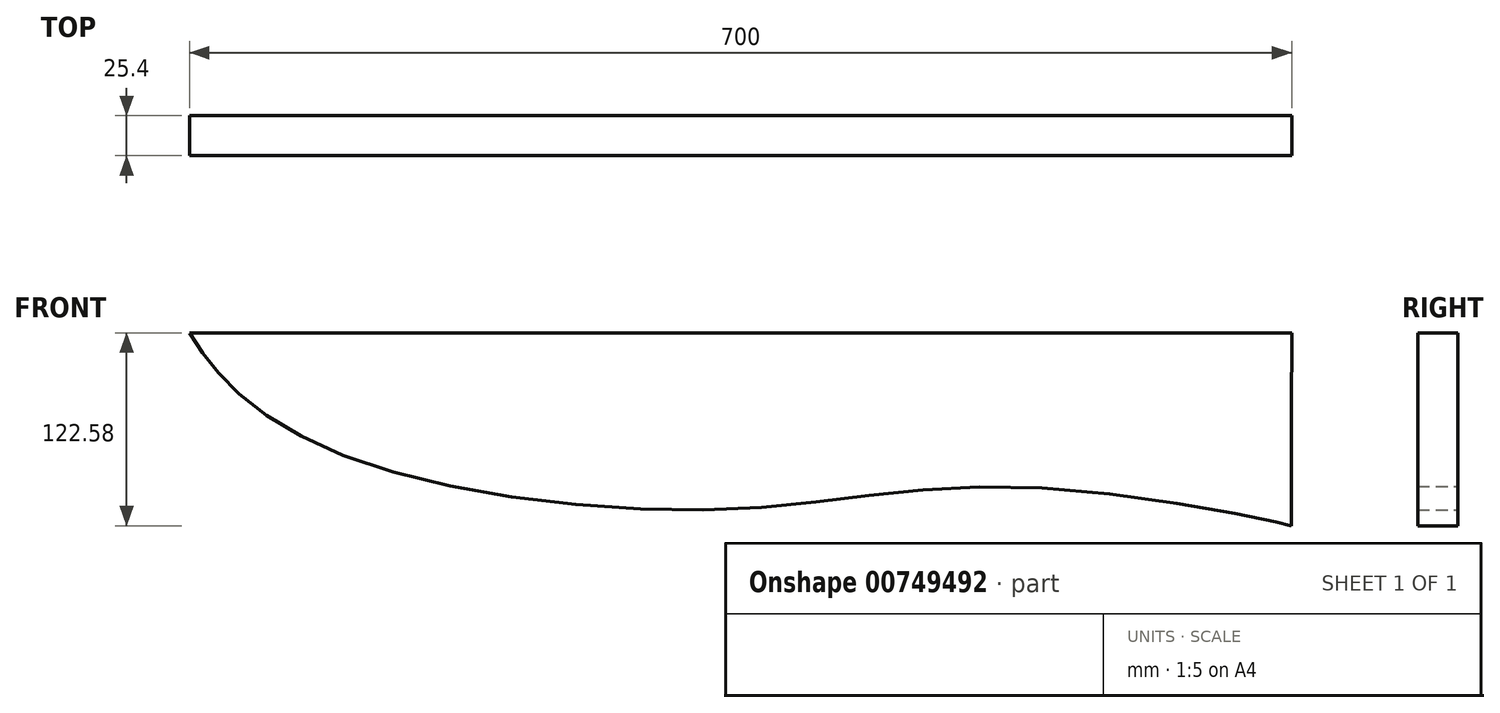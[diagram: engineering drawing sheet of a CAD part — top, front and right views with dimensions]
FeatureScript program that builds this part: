
annotation { "Feature Type Name" : "Feature", "Feature Type Description" : "" }
export const myFeature = defineFeature(function(context is Context, id is Id, definition is map)
    precondition{}
    {
        {
            var Q0;
            Q0=qCreatedBy(makeId("Front.planeOp"),FACE);
            var sketch = newSketch(context, id + "F0", { "sketchPlane" : qUnion([Q0])});
            skLineSegment(sketch, "E0", {"start": v(-359.24, 32.28) * mm, "end": v(340.76, 32.28) * mm});
            skLineSegment(sketch, "E1", {"start": v(340.76, 32.28) * mm, "end": v(340.56, -17.72) * mm});
            skFitSpline(sketch, "E2", {"points": [v(-359.24, 32.28) * mm, v(-334.87, 0) * mm, v(-248.84, -50.24) * mm, v(-15.95, -79.68) * mm, v(181.28, -66.11) * mm, v(340.56, -90.29) * mm, v(340.56, -90.34) * mm], "startDerivative": vector(185.5, -292.89) * mm, "endDerivative": vector(-7.11, -11.54) * mm});
            skLineSegment(sketch, "E3", {"start": v(340.57, -90.32) * mm, "end": v(340.56, -17.72) * mm});
            skSolve(sketch);
        }
        {
            var Q0;
            {var subQ0=sQuery(id+"F0.wireOp",EDGE,"E0");Q0=makeQuery(id+"F0.imprint","IMPRINT",FACE,{"disambiguationData":[TD([[makeQuery(id+"F0.imprint","IMPRINT",EDGE,{"derivedFrom":subQ0}),-1.0]])]});}
            extrude(context, id + "F1", {"entities" : qUnion([Q0]), "depth" : 25.4 * mm, "offsetDistance" : 25.4 * mm});
        }
        {
            var Q0;
            {var subQ0=sQuery(id+"F0.wireOp",EDGE,"E0");Q0=makeQuery(id+"F0.imprint","IMPRINT",FACE,{"disambiguationData":[TD([[makeQuery(id+"F0.imprint","IMPRINT",EDGE,{"derivedFrom":subQ0}),-1.0]])]});}
            extrude(context, id + "F2", {"entities" : qUnion([Q0]), "operationType" : NewBodyOperationType.ADD, "depth" : 5 * mm, "offsetDistance" : 25.4 * mm});
        }
    });
